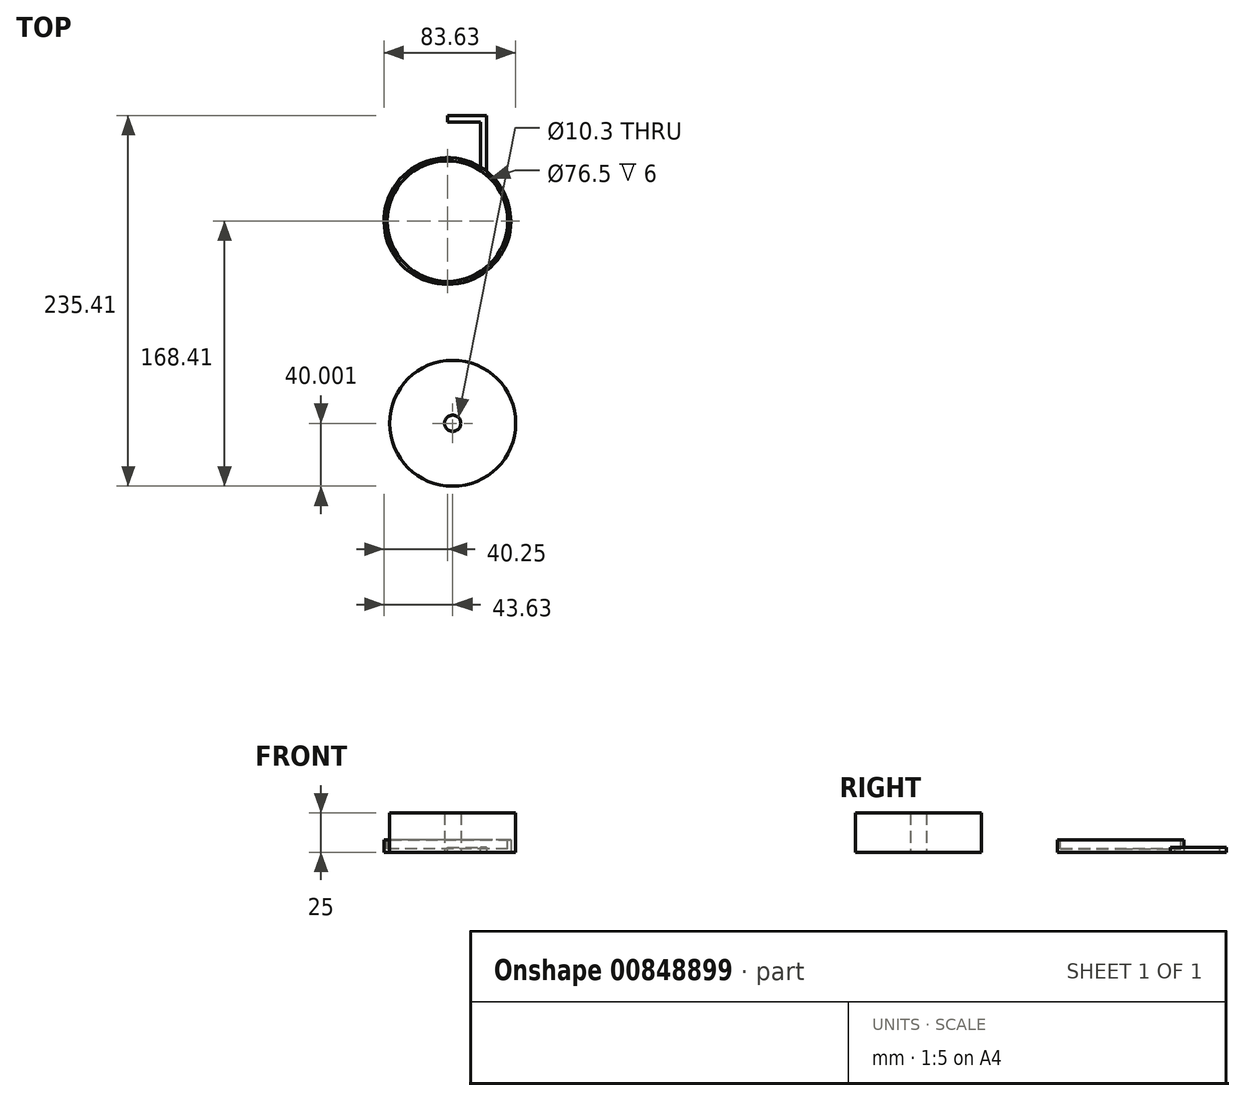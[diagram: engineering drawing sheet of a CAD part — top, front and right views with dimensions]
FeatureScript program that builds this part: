
annotation { "Feature Type Name" : "Feature", "Feature Type Description" : "" }
export const myFeature = defineFeature(function(context is Context, id is Id, definition is map)
    precondition{}
    {
        {
            var Q0;
            Q0=qCreatedBy(makeId("Top.planeOp"),FACE);
            var sketch = newSketch(context, id + "F0", { "sketchPlane" : qUnion([Q0])});
            skCircle(sketch, "E0", {"center": v(0, 0) * mm, "radius": 40.25 * mm});
            skSolve(sketch);
        }
        {
            var Q0;
            Q0=makeQuery(id+"F0.imprint","IMPRINT",FACE,{"disambiguationData":[TD([[makeQuery(id+"F0.imprint","IMPRINT",EDGE,{"derivedFrom":sQuery(id+"F0.wireOp",EDGE,"E0")}),1.0]])]});
            extrude(context, id + "F1", {"entities" : qUnion([Q0]), "depth" : 8 * mm, "offsetDistance" : 25 * mm});
        }
        {
            var Q0;
            Q0=makeQuery(id+"F1.opExtrude","CAP_FACE",FACE,{"disambiguationData":[OSD([sQuery(id+"F0.wireOp",EDGE,"E0")])],"isStart":false});
            var sketch = newSketch(context, id + "F2", { "sketchPlane" : qUnion([Q0])});
            skCircle(sketch, "E1", {"center": v(0, 0) * mm, "radius": 38.25 * mm});
            skSolve(sketch);
        }
        {
            var Q0;
            Q0=makeQuery(id+"F2.imprint","IMPRINT",FACE,{"disambiguationData":[TD([[makeQuery(id+"F2.imprint","IMPRINT",EDGE,{"derivedFrom":sQuery(id+"F2.wireOp",EDGE,"E1")}),1.0]])]});
            extrude(context, id + "F3", {"entities" : qUnion([Q0]), "operationType" : NewBodyOperationType.REMOVE, "depth" : -6 * mm, "offsetDistance" : 25 * mm});
        }
        {
            var Q0;
            Q0=makeQuery(id+"F1.opExtrude","CAP_FACE",FACE,{"disambiguationData":[OSD([sQuery(id+"F0.wireOp",EDGE,"E0")])],"isStart":true});
            var sketch = newSketch(context, id + "F4", { "sketchPlane" : qUnion([Q0])});
            skLineSegment(sketch, "E2.bottom", {"start": v(0, 0) * mm, "end": v(25, 0) * mm});
            skLineSegment(sketch, "E2.top", {"start": v(0, -67) * mm, "end": v(25, -67) * mm});
            skLineSegment(sketch, "E2.left", {"start": v(0, 0) * mm, "end": v(0, -67) * mm});
            skLineSegment(sketch, "E2.right", {"start": v(25, 0) * mm, "end": v(25, -67) * mm});
            skSolve(sketch);
        }
        {
            var Q0;
            {var subQ0=sQuery(id+"F4.wireOp",EDGE,"E2.top");Q0=makeQuery(id+"F4.imprint","IMPRINT",FACE,{"disambiguationData":[TD([[makeQuery(id+"F4.imprint","IMPRINT",EDGE,{"derivedFrom":subQ0}),1.0]])]});}
            extrude(context, id + "F5", {"entities" : qUnion([Q0]), "operationType" : NewBodyOperationType.ADD, "depth" : -3 * mm, "offsetDistance" : 25 * mm});
        }
        {
            var Q0;
            Q0=makeQuery(id+"F5.opExtrude","CAP_FACE",FACE,{"disambiguationData":[OSD([sQuery(id+"F0.wireOp",EDGE,"E0"),sQuery(id+"F4.wireOp",EDGE,"E2.top"),sQuery(id+"F4.wireOp",EDGE,"E2.left"),sQuery(id+"F4.wireOp",EDGE,"E2.right")])],"isStart":false});
            var sketch = newSketch(context, id + "F6", { "sketchPlane" : qUnion([Q0])});
            skLineSegment(sketch, "E3", {"start": v(0, 67) * mm, "end": v(0, 63) * mm});
            skLineSegment(sketch, "E4", {"start": v(0, 63) * mm, "end": v(21, 63) * mm});
            skLineSegment(sketch, "E5", {"start": v(21, 34.34) * mm, "end": v(21, 63) * mm});
            skSolve(sketch);
        }
        {
            var Q0;
            {var subQ0=sQuery(id+"F6.wireOp",EDGE,"E4");Q0=makeQuery(id+"F6.imprint","IMPRINT",FACE,{"disambiguationData":[TD([[makeQuery(id+"F6.imprint","IMPRINT",EDGE,{"derivedFrom":subQ0}),-1.0]])]});}
            var Q1;
            {var subQ0=sQuery(id+"F0.wireOp",EDGE,"E0");Q1=makeQuery(id+"F5.boolean.opBoolean","MERGE",FACE,{"derivedFrom":[makeQuery(id+"F1.opExtrude","CAP_FACE",FACE,{"disambiguationData":[OSD([subQ0])],"isStart":true}),makeQuery(id+"F5.opExtrude","CAP_FACE",FACE,{"disambiguationData":[OSD([subQ0,sQuery(id+"F4.wireOp",EDGE,"E2.top"),sQuery(id+"F4.wireOp",EDGE,"E2.left"),sQuery(id+"F4.wireOp",EDGE,"E2.right")])],"isStart":true})]});}
            extrude(context, id + "F7", {"entities" : qUnion([Q0]), "operationType" : NewBodyOperationType.REMOVE, "endBound" : BoundingType.UP_TO_SURFACE, "oppositeDirection" : true, "depth" : 25 * mm, "endBoundEntityFace" : qUnion([Q1]), "offsetDistance" : 25 * mm});
        }
        {
            var Q0;
            Q0=qCreatedBy(makeId("Top.planeOp"),FACE);
            var sketch = newSketch(context, id + "F8", { "sketchPlane" : qUnion([Q0])});
            skCircle(sketch, "E6", {"center": v(3.38, -128.4) * mm, "radius": 40 * mm});
            skSolve(sketch);
        }
        {
            var Q0;
            Q0=makeQuery(id+"F8.imprint","IMPRINT",FACE,{"disambiguationData":[TD([[makeQuery(id+"F8.imprint","IMPRINT",EDGE,{"derivedFrom":sQuery(id+"F8.wireOp",EDGE,"E6")}),1.0]])]});
            extrude(context, id + "F9", {"entities" : qUnion([Q0]), "depth" : 25 * mm, "offsetDistance" : 25 * mm});
        }
        {
            var Q0;
            Q0=sQuery(id+"F8.wireOp",VERTEX,"E6.center");
            var Q1;
            Q1=makeQuery(id+"F9.opExtrude","SWEPT_BODY",BODY,{"disambiguationData":[OSD([sQuery(id+"F8.wireOp",EDGE,"E6")])]});
            hole(context, id + "F10", {"style" : HoleStyle.SIMPLE, "endStyle" : HoleEndStyle.THROUGH, "oppositeDirection" : true, "standardTappedOrClearance" : lookupTablePath({ "standard" : "ISO", "engagement" : "75%", "pitch" : "1.75 mm", "size" : "M12", "type" : "Tapped" }), "standardBlindInLast" : lookupTablePath({ "standard" : "ISO", "engagement" : "75%", "pitch" : "1.75 mm", "size" : "M12", "type" : "Tapped" }), "holeDiameter" : 10.3 * mm, "majorDiameter" : 12 * mm, "showTappedDepth" : true, "isTappedThrough" : true, "tappedDepth" : 12 * mm, "tapClearance" : 3, "startFromSketch" : true, "locations" : qUnion([Q0]), "scope" : qUnion([Q1])});
        }
    });
